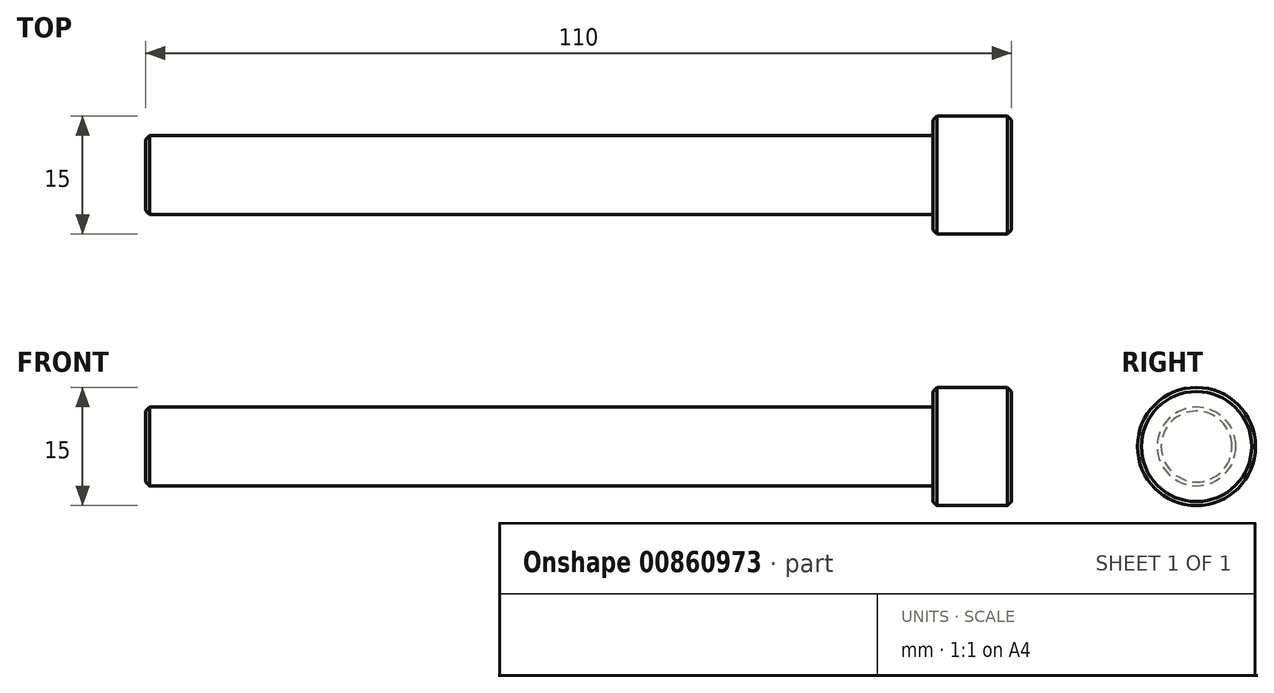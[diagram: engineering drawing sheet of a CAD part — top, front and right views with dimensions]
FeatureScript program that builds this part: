
annotation { "Feature Type Name" : "Feature", "Feature Type Description" : "" }
export const myFeature = defineFeature(function(context is Context, id is Id, definition is map)
    precondition{}
    {
        {
            var Q0;
            Q0=qCreatedBy(makeId("Right.planeOp"),FACE);
            var sketch = newSketch(context, id + "F0", { "sketchPlane" : qUnion([Q0])});
            skCircle(sketch, "E0", {"center": v(0, 0) * mm, "radius": 5 * mm});
            skSolve(sketch);
        }
        {
            var Q0;
            Q0=makeQuery(id+"F0.imprint","IMPRINT",FACE,{"disambiguationData":[TD([[makeQuery(id+"F0.imprint","IMPRINT",EDGE,{"derivedFrom":sQuery(id+"F0.wireOp",EDGE,"E0")}),1.0]])]});
            extrude(context, id + "F1", {"entities" : qUnion([Q0]), "oppositeDirection" : true, "depth" : 100 * mm, "offsetDistance" : 25 * mm});
        }
        {
            var Q0;
            Q0=qCreatedBy(makeId("Right.planeOp"),FACE);
            var sketch = newSketch(context, id + "F2", { "sketchPlane" : qUnion([Q0])});
            skCircle(sketch, "E1", {"center": v(0, 0) * mm, "radius": 7.5 * mm});
            skSolve(sketch);
        }
        {
            var Q0;
            Q0=makeQuery(id+"F2.imprint","IMPRINT",FACE,{"disambiguationData":[TD([[makeQuery(id+"F2.imprint","IMPRINT",EDGE,{"derivedFrom":sQuery(id+"F2.wireOp",EDGE,"E1")}),1.0]])]});
            extrude(context, id + "F3", {"entities" : qUnion([Q0]), "operationType" : NewBodyOperationType.ADD, "depth" : 10 * mm, "offsetDistance" : 25 * mm});
        }
        {
            var Q0;
            Q0=makeQuery(id+"F3.opExtrude","CAP_EDGE",EDGE,{"disambiguationData":[OSD([sQuery(id+"F2.wireOp",EDGE,"E1")])],"isStart":false});
            var Q1;
            Q1=makeQuery(id+"F1.opExtrude","CAP_EDGE",EDGE,{"disambiguationData":[OSD([sQuery(id+"F0.wireOp",EDGE,"E0")])],"isStart":false});
            var Q2;
            Q2=makeQuery(id+"F3.opExtrude","CAP_EDGE",EDGE,{"disambiguationData":[OSD([sQuery(id+"F2.wireOp",EDGE,"E1")])],"isStart":true});
            chamfer(context, id + "F4", {"entities" : qUnion([Q0, Q1, Q2]), "width" : 0.5 * mm, "tangentPropagation" : true});
        }
    });
